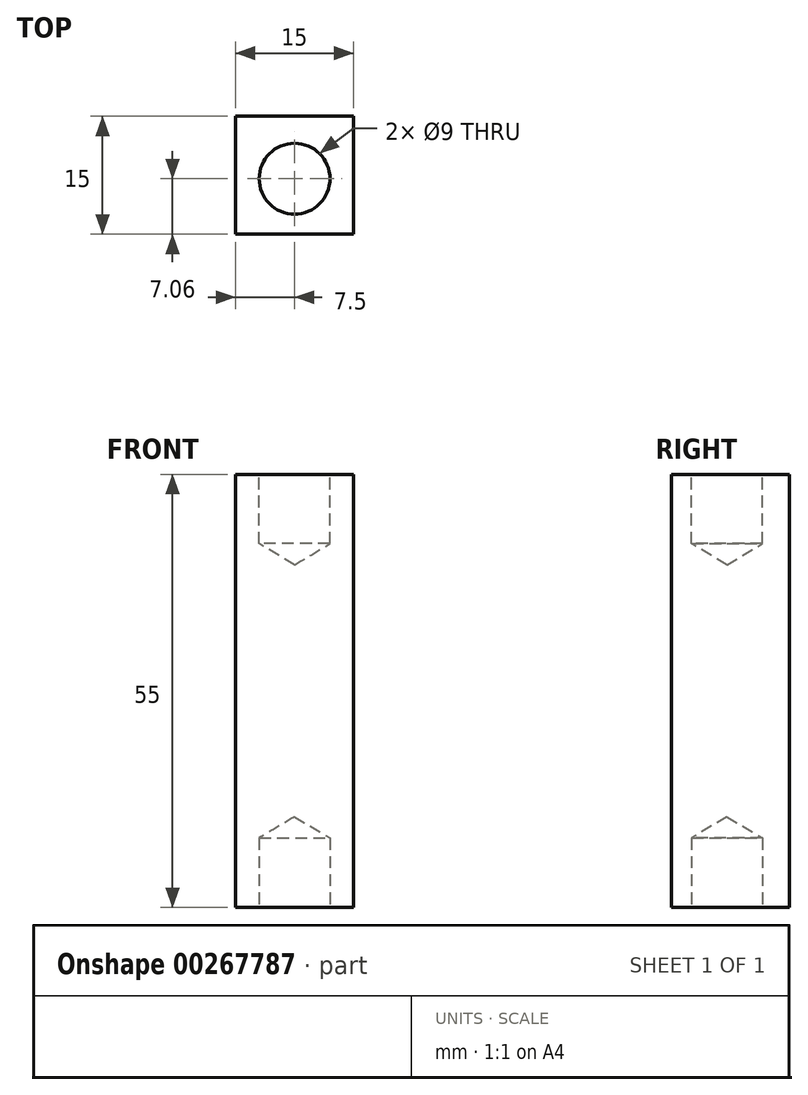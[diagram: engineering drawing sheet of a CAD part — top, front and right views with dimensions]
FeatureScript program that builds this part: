
annotation { "Feature Type Name" : "Feature", "Feature Type Description" : "" }
export const myFeature = defineFeature(function(context is Context, id is Id, definition is map)
    precondition{}
    {
        {
            var Q0;
            Q0=qCreatedBy(makeId("Top.planeOp"),FACE);
            var sketch = newSketch(context, id + "F0", { "sketchPlane" : qUnion([Q0])});
            skLineSegment(sketch, "E0.bottom", {"start": v(7.5, 7.94) * mm, "end": v(-7.5, 7.94) * mm});
            skLineSegment(sketch, "E0.top", {"start": v(7.5, -7.06) * mm, "end": v(-7.5, -7.06) * mm});
            skLineSegment(sketch, "E0.left", {"start": v(7.5, 7.94) * mm, "end": v(7.5, -7.06) * mm});
            skLineSegment(sketch, "E0.right", {"start": v(-7.5, 7.94) * mm, "end": v(-7.5, -7.06) * mm});
            skPoint(sketch, "E0.middle", {"position": v(0, 0.44) * mm});
            skSolve(sketch);
        }
        {
            var Q0;
            Q0=makeQuery(id+"F0.imprint","IMPRINT",FACE,{"disambiguationData":[TD([[makeQuery(id+"F0.imprint","IMPRINT",EDGE,{"derivedFrom":sQuery(id+"F0.wireOp",EDGE,"E0.bottom")}),1.0]])]});
            extrude(context, id + "F1", {"entities" : qUnion([Q0]), "depth" : 55 * mm});
        }
        {
            var Q0;
            Q0=makeQuery(id+"F1.opExtrude","CAP_FACE",FACE,{"disambiguationData":[OSD([sQuery(id+"F0.wireOp",EDGE,"E0.bottom"),sQuery(id+"F0.wireOp",EDGE,"E0.top"),sQuery(id+"F0.wireOp",EDGE,"E0.left"),sQuery(id+"F0.wireOp",EDGE,"E0.right")])],"isStart":true});
            var sketch = newSketch(context, id + "F2", { "sketchPlane" : qUnion([Q0])});
            skCircle(sketch, "E1", {"center": v(0, 0) * mm, "radius": 4.1 * mm});
            skSolve(sketch);
        }
        {
            var Q0;
            Q0=makeQuery(id+"F1.opExtrude","CAP_FACE",FACE,{"disambiguationData":[OSD([sQuery(id+"F0.wireOp",EDGE,"E0.bottom"),sQuery(id+"F0.wireOp",EDGE,"E0.top"),sQuery(id+"F0.wireOp",EDGE,"E0.left"),sQuery(id+"F0.wireOp",EDGE,"E0.right")])],"isStart":false});
            var sketch = newSketch(context, id + "F3", { "sketchPlane" : qUnion([Q0])});
            skCircle(sketch, "E2", {"center": v(0, 0) * mm, "radius": 4.1 * mm});
            skSolve(sketch);
        }
        {
            var Q0;
            Q0=sQuery(id+"F2.wireOp",VERTEX,"E1.center");
            var Q1;
            Q1=makeQuery(id+"F1.opExtrude","SWEPT_BODY",BODY,{"disambiguationData":[OSD([sQuery(id+"F0.wireOp",EDGE,"E0.bottom"),sQuery(id+"F0.wireOp",EDGE,"E0.top"),sQuery(id+"F0.wireOp",EDGE,"E0.left"),sQuery(id+"F0.wireOp",EDGE,"E0.right")])]});
            hole(context, id + "F4", {"style" : HoleStyle.SIMPLE, "endStyle" : HoleEndStyle.BLIND, "holeDiameter" : 9 * mm, "holeDepth" : 8.8 * mm, "tappedDepth" : 12 * mm, "tapClearance" : 3, "startFromSketch" : true, "locations" : qUnion([Q0]), "scope" : qUnion([Q1])});
        }
        {
            var Q0;
            Q0=sQuery(id+"F3.wireOp",VERTEX,"E2.center");
            var Q1;
            Q1=makeQuery(id+"F1.opExtrude","SWEPT_BODY",BODY,{"disambiguationData":[OSD([sQuery(id+"F0.wireOp",EDGE,"E0.bottom"),sQuery(id+"F0.wireOp",EDGE,"E0.top"),sQuery(id+"F0.wireOp",EDGE,"E0.left"),sQuery(id+"F0.wireOp",EDGE,"E0.right")])]});
            hole(context, id + "F5", {"style" : HoleStyle.SIMPLE, "endStyle" : HoleEndStyle.BLIND, "holeDiameter" : 9 * mm, "holeDepth" : 8.8 * mm, "tappedDepth" : 12 * mm, "tapClearance" : 3, "startFromSketch" : true, "locations" : qUnion([Q0]), "scope" : qUnion([Q1])});
        }
    });
